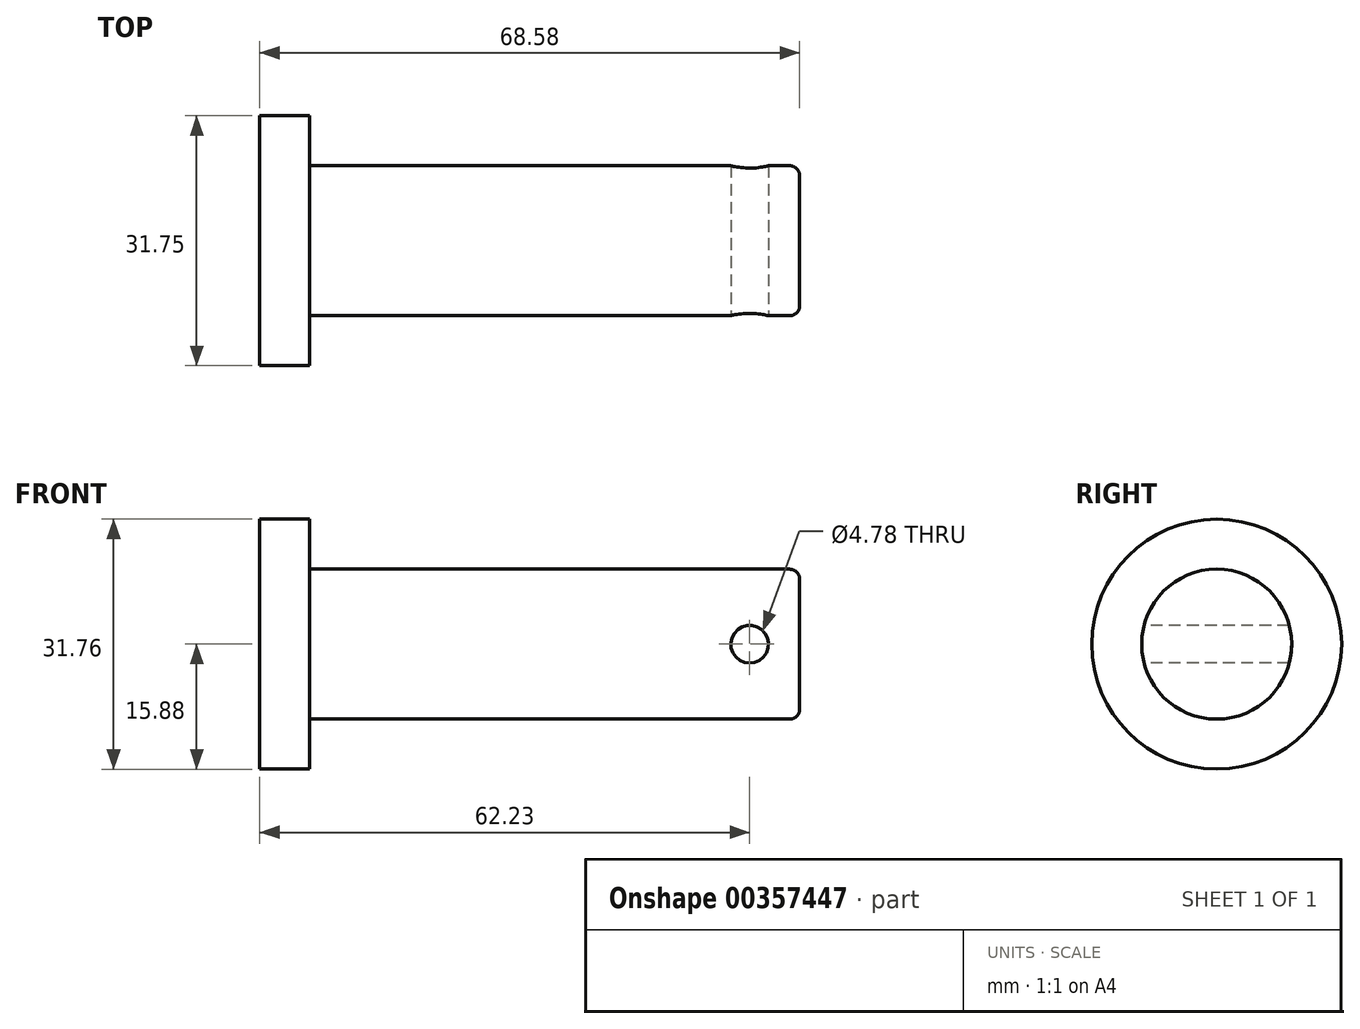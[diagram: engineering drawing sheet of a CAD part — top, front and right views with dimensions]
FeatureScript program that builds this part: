
annotation { "Feature Type Name" : "Feature", "Feature Type Description" : "" }
export const myFeature = defineFeature(function(context is Context, id is Id, definition is map)
    precondition{}
    {
        {
            var Q0;
            Q0=qCreatedBy(makeId("Right.planeOp"),FACE);
            var sketch = newSketch(context, id + "F0", { "sketchPlane" : qUnion([Q0])});
            skCircle(sketch, "E0", {"center": v(15.88, 0) * mm, "radius": 15.88 * mm});
            skSolve(sketch);
        }
        {
            var Q0;
            Q0=makeQuery(id+"F0.imprint","IMPRINT",FACE,{"disambiguationData":[TD([[makeQuery(id+"F0.imprint","IMPRINT",EDGE,{"derivedFrom":sQuery(id+"F0.wireOp",EDGE,"E0")}),1.0]])]});
            extrude(context, id + "F1", {"entities" : qUnion([Q0]), "depth" : 6.35 * mm});
        }
        {
            var Q0;
            Q0=makeQuery(id+"F1.opExtrude","CAP_FACE",FACE,{"disambiguationData":[OSD([sQuery(id+"F0.wireOp",EDGE,"E0")])],"isStart":false});
            var sketch = newSketch(context, id + "F2", { "sketchPlane" : qUnion([Q0])});
            skCircle(sketch, "E1", {"center": v(15.88, 0) * mm, "radius": 9.53 * mm});
            skSolve(sketch);
        }
        {
            var Q0;
            Q0=makeQuery(id+"F2.imprint","IMPRINT",FACE,{"disambiguationData":[TD([[makeQuery(id+"F2.imprint","IMPRINT",EDGE,{"derivedFrom":sQuery(id+"F2.wireOp",EDGE,"E1")}),1.0]])]});
            extrude(context, id + "F3", {"entities" : qUnion([Q0]), "operationType" : NewBodyOperationType.ADD, "depth" : 62.23 * mm});
        }
        {
            var Q0;
            Q0=makeQuery(id+"F3.opExtrude","CAP_EDGE",EDGE,{"disambiguationData":[OSD([sQuery(id+"F2.wireOp",EDGE,"E1")])],"isStart":false});
            fillet(context, id + "F4", {"entities" : qUnion([Q0]), "radius" : 1.27 * mm, "tangentPropagation" : true, "allowEdgeOverflow" : false});
        }
        {
            var Q0;
            Q0=qCreatedBy(makeId("Front.planeOp"),FACE);
            var sketch = newSketch(context, id + "F5", { "sketchPlane" : qUnion([Q0])});
            skCircle(sketch, "E2", {"center": v(62.23, 0) * mm, "radius": 2.39 * mm});
            skSolve(sketch);
        }
        {
            var Q0;
            Q0=makeQuery(id+"F5.imprint","IMPRINT",FACE,{"disambiguationData":[TD([[makeQuery(id+"F5.imprint","IMPRINT",EDGE,{"derivedFrom":sQuery(id+"F5.wireOp",EDGE,"E2")}),1.0]])]});
            extrude(context, id + "F6", {"entities" : qUnion([Q0]), "operationType" : NewBodyOperationType.REMOVE, "oppositeDirection" : true, "depth" : 50.8 * mm});
        }
    });
